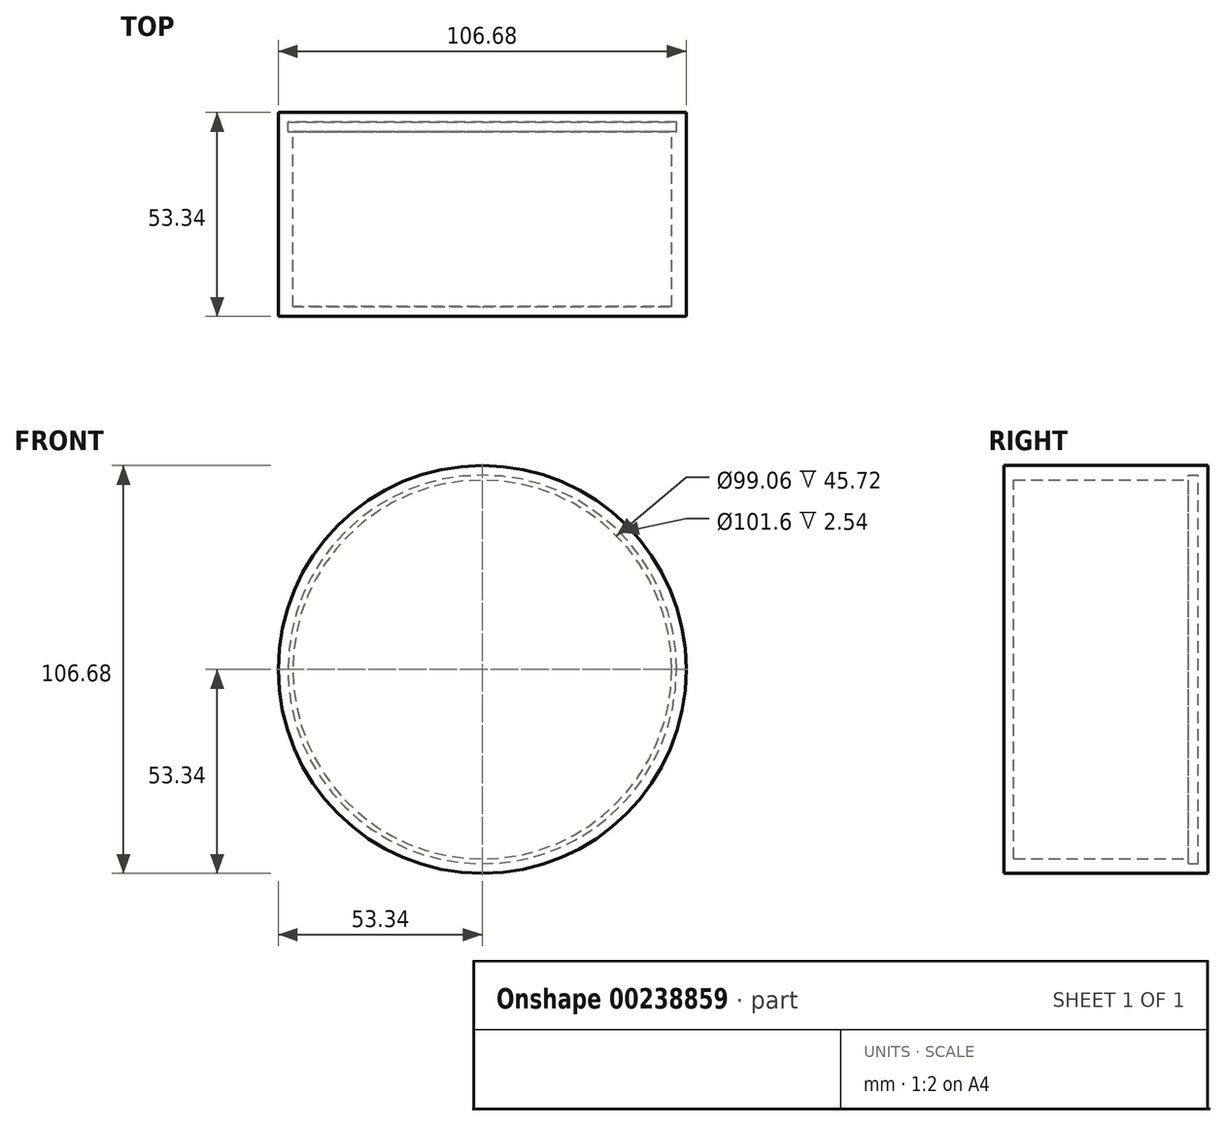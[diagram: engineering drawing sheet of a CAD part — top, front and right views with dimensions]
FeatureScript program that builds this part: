
annotation { "Feature Type Name" : "Feature", "Feature Type Description" : "" }
export const myFeature = defineFeature(function(context is Context, id is Id, definition is map)
    precondition{}
    {
        {
            var Q0;
            Q0=qCreatedBy(makeId("Front.planeOp"),FACE);
            var sketch = newSketch(context, id + "F2", { "sketchPlane" : qUnion([Q0])});
            skCircle(sketch, "E0", {"center": v(0, 0) * mm, "radius": 52.07 * mm});
            skCircle(sketch, "E1", {"center": v(0, 0) * mm, "radius": 53.34 * mm});
            skSolve(sketch);
        }
        {
            var Q0;
            Q0=makeQuery(id+"F2.imprint","IMPRINT",FACE,{"disambiguationData":[TD([[makeQuery(id+"F2.imprint","IMPRINT",EDGE,{"derivedFrom":sQuery(id+"F2.wireOp",EDGE,"E0")}),1.0]])]});
            extrude(context, id + "F3", {"entities" : qUnion([Q0]), "depth" : 50.8 * mm});
        }
        {
            var Q0;
            Q0=makeQuery(id+"F2.imprint","IMPRINT",FACE,{"disambiguationData":[TD([[makeQuery(id+"F2.imprint","IMPRINT",EDGE,{"derivedFrom":sQuery(id+"F2.wireOp",EDGE,"E0")}),-1.0]])]});
            extrude(context, id + "F0", {"entities" : qUnion([Q0]), "operationType" : NewBodyOperationType.ADD, "depth" : 7.62 * mm});
        }
        {
            var Q0;
            Q0=makeQuery(id+"F0.opExtrude","CAP_FACE",FACE,{"disambiguationData":[OSD([sQuery(id+"F2.wireOp",EDGE,"E0"),sQuery(id+"F2.wireOp",EDGE,"E1")])],"isStart":false});
            extrude(context, id + "F1", {"entities" : qUnion([Q0]), "depth" : 43.18 * mm});
        }
        {
            var Q0;
            Q0=makeQuery(id+"F3.opExtrude","CAP_FACE",FACE,{"disambiguationData":[OSD([sQuery(id+"F2.wireOp",EDGE,"E0")])],"isStart":false});
            shell(context, id + "F4", {"entities" : qUnion([Q0]), "thickness" : 2.54 * mm});
        }
        {
            var Q0;
            Q0=makeQuery(id+"F1.opExtrude","CAP_FACE",FACE,{"disambiguationData":[OSD([sQuery(id+"F2.wireOp",EDGE,"E0"),sQuery(id+"F2.wireOp",EDGE,"E1")])],"isStart":false});
            var sketch = newSketch(context, id + "F5", { "sketchPlane" : qUnion([Q0])});
            skCircle(sketch, "E2.0", {"center": v(0, 0) * mm, "radius": 53.34 * mm});
            skSolve(sketch);
        }
        {
            var Q0;
            Q0 = qSketchRegion(id + "F5", true);
            extrude(context, id + "F6", {"entities" : qUnion([Q0]), "operationType" : NewBodyOperationType.ADD, "depth" : 2.54 * mm});
        }
    });
